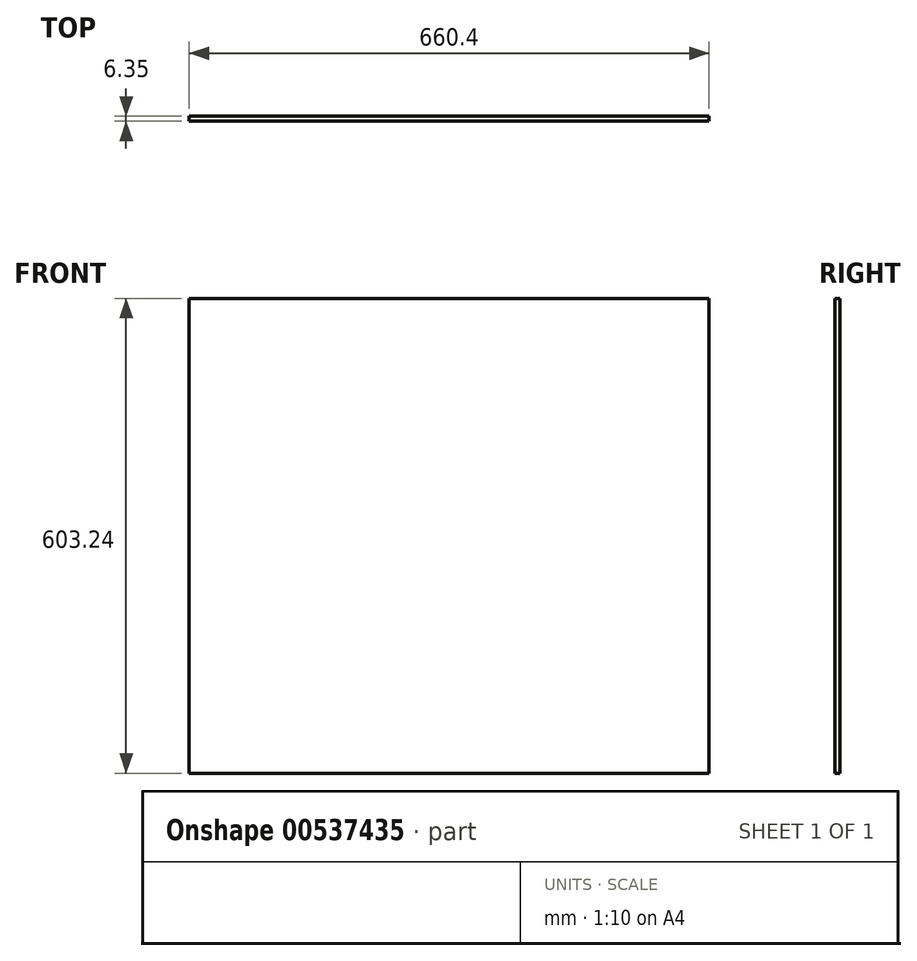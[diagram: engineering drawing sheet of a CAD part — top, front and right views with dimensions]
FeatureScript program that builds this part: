
annotation { "Feature Type Name" : "Feature", "Feature Type Description" : "" }
export const myFeature = defineFeature(function(context is Context, id is Id, definition is map)
    precondition{}
    {
        {
            var Q0;
            Q0=qCreatedBy(makeId("Front.planeOp"),FACE);
            var sketch = newSketch(context, id + "F0", { "sketchPlane" : qUnion([Q0])});
            skLineSegment(sketch, "E0.bottom", {"start": v(330.2, 301.63) * mm, "end": v(-330.2, 301.63) * mm});
            skLineSegment(sketch, "E0.top", {"start": v(330.2, -301.63) * mm, "end": v(-330.2, -301.63) * mm});
            skLineSegment(sketch, "E0.left", {"start": v(330.2, 301.63) * mm, "end": v(330.2, -301.63) * mm});
            skLineSegment(sketch, "E0.right", {"start": v(-330.2, 301.63) * mm, "end": v(-330.2, -301.63) * mm});
            skPoint(sketch, "E0.middle", {"position": v(0, 0) * mm});
            skSolve(sketch);
        }
        {
            var Q0;
            Q0=makeQuery(id+"F0.imprint","IMPRINT",FACE,{"disambiguationData":[TD([[makeQuery(id+"F0.imprint","IMPRINT",EDGE,{"derivedFrom":sQuery(id+"F0.wireOp",EDGE,"E0.bottom")}),1.0]])]});
            extrude(context, id + "F1", {"entities" : qUnion([Q0]), "depth" : 6.35 * mm, "offsetDistance" : 25.4 * mm});
        }
    });
